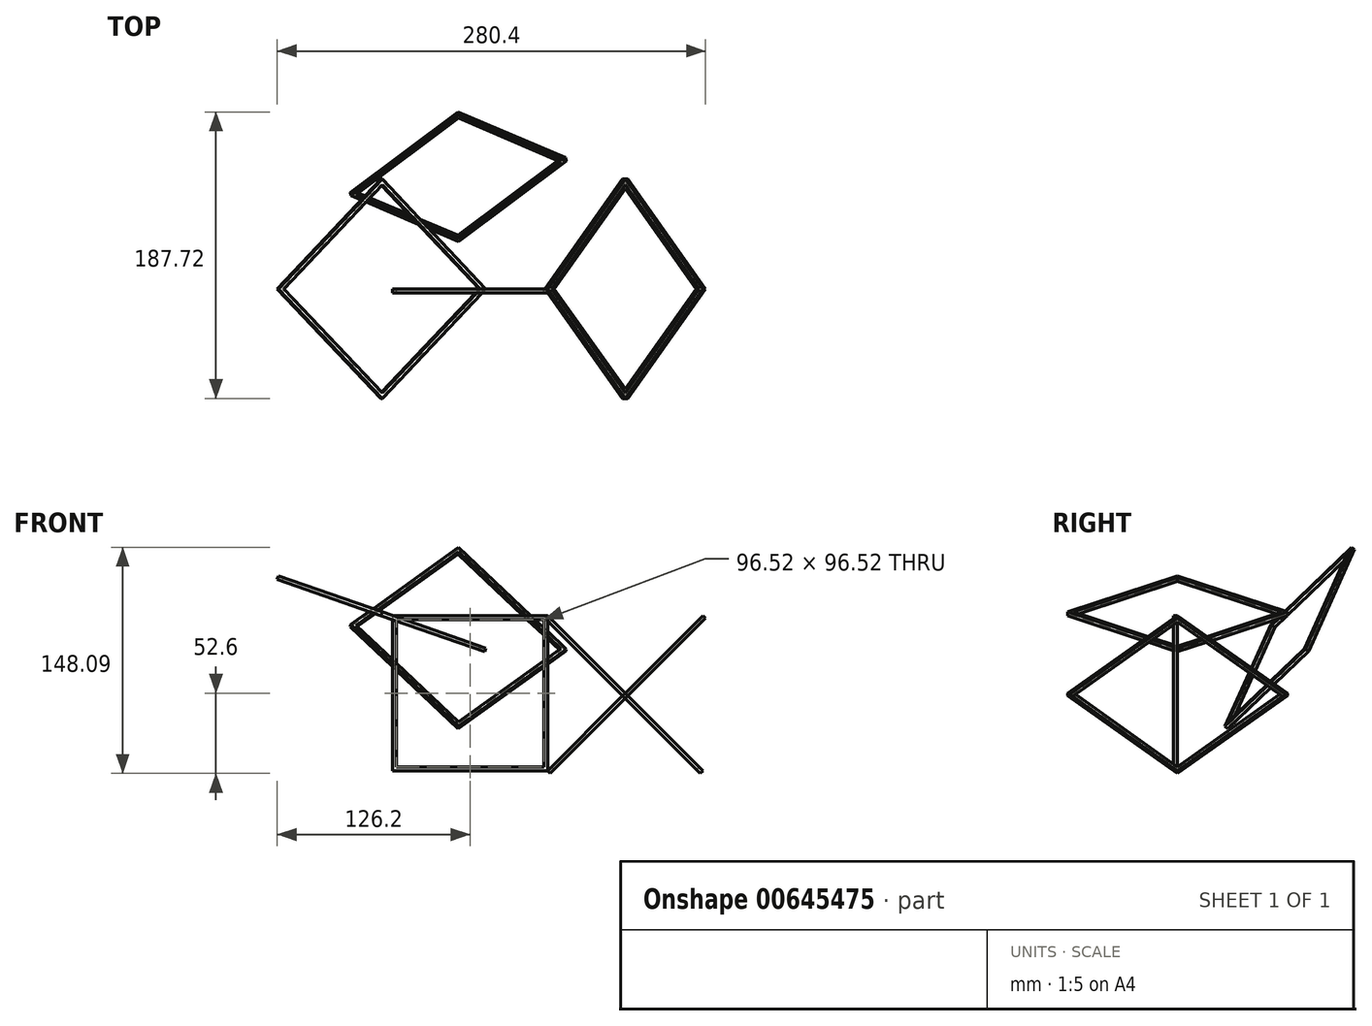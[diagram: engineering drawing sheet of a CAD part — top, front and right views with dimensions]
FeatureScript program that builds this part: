
annotation { "Feature Type Name" : "Feature", "Feature Type Description" : "" }
export const myFeature = defineFeature(function(context is Context, id is Id, definition is map)
    precondition{}
    {
        {
            var Q0;
            Q0=qCreatedBy(makeId("Front.planeOp"),FACE);
            var sketch = newSketch(context, id + "F0", { "sketchPlane" : qUnion([Q0])});
            skLineSegment(sketch, "E0.bottom", {"start": v(-48.26, 48.26) * mm, "end": v(48.26, 48.26) * mm});
            skLineSegment(sketch, "E0.top", {"start": v(-48.26, -48.26) * mm, "end": v(48.26, -48.26) * mm});
            skLineSegment(sketch, "E0.left", {"start": v(-48.26, 48.26) * mm, "end": v(-48.26, -48.26) * mm});
            skLineSegment(sketch, "E0.right", {"start": v(48.26, 48.26) * mm, "end": v(48.26, -48.26) * mm});
            skPoint(sketch, "E0.middle", {"position": v(0, 0) * mm});
            skLineSegment(sketch, "E1.bottom", {"start": v(-50.8, 50.8) * mm, "end": v(50.8, 50.8) * mm});
            skLineSegment(sketch, "E1.top", {"start": v(-50.8, -50.8) * mm, "end": v(50.8, -50.8) * mm});
            skLineSegment(sketch, "E1.left", {"start": v(-50.8, 50.8) * mm, "end": v(-50.8, -50.8) * mm});
            skLineSegment(sketch, "E1.right", {"start": v(50.8, 50.8) * mm, "end": v(50.8, -50.8) * mm});
            skSolve(sketch);
        }
        {
            var Q0;
            Q0=makeQuery(id+"F0.imprint","IMPRINT",FACE,{"disambiguationData":[TD([[makeQuery(id+"F0.imprint","IMPRINT",EDGE,{"derivedFrom":sQuery(id+"F0.wireOp",EDGE,"E0.bottom")}),1.0]])]});
            extrude(context, id + "F1", {"entities" : qUnion([Q0]), "depth" : 2.54 * mm, "offsetDistance" : 25.4 * mm});
        }
        {
            var Q0;
            Q0=makeQuery(id+"F1.opExtrude","SWEPT_EDGE",EDGE,{"disambiguationData":[OSD([sQuery(id+"F0.wireOp",EDGE,"E1.bottom"),sQuery(id+"F0.wireOp",EDGE,"E1.right")])]});
            cPlane(context, id + "F2", {"entities" : qUnion([Q0]), "cplaneType" : CPlaneType.LINE_ANGLE, "offset" : 25.4 * mm, "angle" : 45 * degree, "width" : 152.4 * mm, "height" : 152.4 * mm});
        }
        {
            var Q0;
            Q0=qCreatedBy(id+"F2.planeOp",FACE);
            var sketch = newSketch(context, id + "F3", { "sketchPlane" : qUnion([Q0])});
            skLineSegment(sketch, "E2", {"start": v(0, 0) * mm, "end": v(-71.84, -71.84) * mm});
            skLineSegment(sketch, "E3", {"start": v(-71.84, -71.84) * mm, "end": v(0, -143.68) * mm});
            skLineSegment(sketch, "E4", {"start": v(0, -143.68) * mm, "end": v(71.84, -71.84) * mm});
            skLineSegment(sketch, "E5", {"start": v(71.84, -71.84) * mm, "end": v(0, 0) * mm});
            skLineSegment(sketch, "E6", {"start": v(-68.25, -71.84) * mm, "end": v(0, -140.1) * mm});
            skLineSegment(sketch, "E7", {"start": v(0, -140.1) * mm, "end": v(68.25, -71.84) * mm});
            skLineSegment(sketch, "E8", {"start": v(68.25, -71.84) * mm, "end": v(0, -3.6) * mm});
            skLineSegment(sketch, "E9", {"start": v(0, -3.6) * mm, "end": v(-68.25, -71.84) * mm});
            skSolve(sketch);
        }
        {
            var Q0;
            Q0=makeQuery(id+"F3.imprint","IMPRINT",FACE,{"disambiguationData":[TD([[makeQuery(id+"F3.imprint","IMPRINT",EDGE,{"derivedFrom":sQuery(id+"F3.wireOp",EDGE,"E2")}),1.0]])]});
            extrude(context, id + "F4", {"entities" : qUnion([Q0]), "oppositeDirection" : true, "depth" : 2.54 * mm, "offsetDistance" : 25.4 * mm});
        }
        {
            var Q0;
            Q0=makeQuery(id+"F1.opExtrude","CAP_VERTEX",VERTEX,{"disambiguationData":[OSD([sQuery(id+"F0.wireOp",EDGE,"E1.bottom"),sQuery(id+"F0.wireOp",EDGE,"E1.left")])],"isStart":true});
            var Q1;
            Q1=makeQuery(id+"F1.opExtrude","CAP_VERTEX",VERTEX,{"disambiguationData":[OSD([sQuery(id+"F0.wireOp",EDGE,"E1.bottom"),sQuery(id+"F0.wireOp",EDGE,"E1.left")])],"isStart":false});
            var Q2;
            Q2=makeQuery(id+"F4.opExtrude","CAP_VERTEX",VERTEX,{"disambiguationData":[OSD([sQuery(id+"F3.wireOp",EDGE,"E2"),sQuery(id+"F3.wireOp",EDGE,"E3")])],"isStart":false});
            cPlane(context, id + "F5", {"entities" : qUnion([Q0, Q1, Q2]), "cplaneType" : CPlaneType.THREE_POINT, "offset" : 25.4 * mm, "width" : 152.4 * mm, "height" : 152.4 * mm});
        }
        {
            var Q0;
            Q0=qCreatedBy(id+"F5.planeOp",FACE);
            var sketch = newSketch(context, id + "F6", { "sketchPlane" : qUnion([Q0])});
            skLineSegment(sketch, "E10", {"start": v(-71.84, 71.84) * mm, "end": v(-143.68, 0) * mm});
            skLineSegment(sketch, "E11", {"start": v(-143.68, 0) * mm, "end": v(-71.84, -71.84) * mm});
            skLineSegment(sketch, "E12", {"start": v(-71.84, -71.84) * mm, "end": v(0, 0) * mm});
            skLineSegment(sketch, "E13", {"start": v(0, 0) * mm, "end": v(-71.84, 71.84) * mm});
            skLineSegment(sketch, "E14", {"start": v(-140.1, 0) * mm, "end": v(-71.84, -68.25) * mm});
            skLineSegment(sketch, "E15", {"start": v(-71.84, -68.25) * mm, "end": v(-3.6, 0) * mm});
            skLineSegment(sketch, "E16", {"start": v(-3.6, 0) * mm, "end": v(-71.84, 68.25) * mm});
            skLineSegment(sketch, "E17", {"start": v(-71.84, 68.25) * mm, "end": v(-140.1, 0) * mm});
            skSolve(sketch);
        }
        {
            var Q0;
            Q0 = qSketchRegion(id + "F6", true);
            extrude(context, id + "F7", {"entities" : qUnion([Q0]), "depth" : 2.54 * mm, "offsetDistance" : 25.4 * mm});
        }
        {
            var Q0;
            Q0=makeQuery(id+"F4.opExtrude","CAP_VERTEX",VERTEX,{"disambiguationData":[OSD([sQuery(id+"F3.wireOp",EDGE,"E4"),sQuery(id+"F3.wireOp",EDGE,"E5")])],"isStart":false});
            var Q1;
            Q1=makeQuery(id+"F4.opExtrude","CAP_VERTEX",VERTEX,{"disambiguationData":[OSD([sQuery(id+"F3.wireOp",EDGE,"E4"),sQuery(id+"F3.wireOp",EDGE,"E5")])],"isStart":true});
            var Q2;
            Q2=makeQuery(id+"F1.opExtrude","CAP_VERTEX",VERTEX,{"disambiguationData":[OSD([sQuery(id+"F0.wireOp",EDGE,"E1.top"),sQuery(id+"F0.wireOp",EDGE,"E1.right")])],"isStart":true});
            cPlane(context, id + "F8", {"entities" : qUnion([Q0, Q1, Q2]), "cplaneType" : CPlaneType.THREE_POINT, "offset" : 25.4 * mm, "width" : 152.4 * mm, "height" : 152.4 * mm});
        }
        {
            var Q0;
            Q0=qCreatedBy(id+"F8.planeOp",FACE);
            var sketch = newSketch(context, id + "F9", { "sketchPlane" : qUnion([Q0])});
            skLineSegment(sketch, "E18", {"start": v(0, 143.68) * mm, "end": v(-71.84, 71.84) * mm});
            skLineSegment(sketch, "E19", {"start": v(-71.84, 71.84) * mm, "end": v(0, 0) * mm});
            skLineSegment(sketch, "E20", {"start": v(0, 0) * mm, "end": v(71.84, 71.84) * mm});
            skLineSegment(sketch, "E21", {"start": v(71.84, 71.84) * mm, "end": v(0, 143.68) * mm});
            skLineSegment(sketch, "E22", {"start": v(-68.25, 71.84) * mm, "end": v(0, 3.6) * mm});
            skLineSegment(sketch, "E23", {"start": v(0, 3.6) * mm, "end": v(68.25, 71.84) * mm});
            skLineSegment(sketch, "E24", {"start": v(68.25, 71.84) * mm, "end": v(0, 140.1) * mm});
            skLineSegment(sketch, "E25", {"start": v(0, 140.1) * mm, "end": v(-68.25, 71.84) * mm});
            skSolve(sketch);
        }
        {
            var Q0;
            Q0=makeQuery(id+"F9.imprint","IMPRINT",FACE,{"disambiguationData":[TD([[makeQuery(id+"F9.imprint","IMPRINT",EDGE,{"derivedFrom":sQuery(id+"F9.wireOp",EDGE,"E18")}),1.0]])]});
            extrude(context, id + "F10", {"entities" : qUnion([Q0]), "oppositeDirection" : true, "depth" : 2.54 * mm, "offsetDistance" : 25.4 * mm});
        }
        {
            var Q0;
            Q0=makeQuery(id+"F7.opExtrude","CAP_VERTEX",VERTEX,{"disambiguationData":[OSD([sQuery(id+"F6.wireOp",EDGE,"E11"),sQuery(id+"F6.wireOp",EDGE,"E12")])],"isStart":true});
            var Q1;
            Q1=makeQuery(id+"F10.opExtrude","CAP_VERTEX",VERTEX,{"disambiguationData":[OSD([sQuery(id+"F9.wireOp",EDGE,"E18"),sQuery(id+"F9.wireOp",EDGE,"E19")])],"isStart":false});
            var Q2;
            Q2=makeQuery(id+"F1.opExtrude","CAP_VERTEX",VERTEX,{"disambiguationData":[OSD([sQuery(id+"F0.wireOp",EDGE,"E1.top"),sQuery(id+"F0.wireOp",EDGE,"E1.left")])],"isStart":true});
            cPlane(context, id + "F11", {"entities" : qUnion([Q0, Q1, Q2]), "cplaneType" : CPlaneType.THREE_POINT, "offset" : 25.4 * mm, "width" : 152.4 * mm, "height" : 152.4 * mm});
        }
        {
            var Q0;
            Q0=qCreatedBy(id+"F11.planeOp",FACE);
            var sketch = newSketch(context, id + "F12", { "sketchPlane" : qUnion([Q0])});
            skLineSegment(sketch, "E26", {"start": v(0, 143.68) * mm, "end": v(-71.84, 71.84) * mm});
            skLineSegment(sketch, "E27", {"start": v(-71.84, 71.84) * mm, "end": v(0, 0) * mm});
            skLineSegment(sketch, "E28", {"start": v(0, 0) * mm, "end": v(71.84, 71.84) * mm});
            skLineSegment(sketch, "E29", {"start": v(71.84, 71.84) * mm, "end": v(0, 143.68) * mm});
            skLineSegment(sketch, "E30", {"start": v(-68.25, 71.84) * mm, "end": v(0, 3.6) * mm});
            skLineSegment(sketch, "E31", {"start": v(0, 3.6) * mm, "end": v(68.25, 71.84) * mm});
            skLineSegment(sketch, "E32", {"start": v(68.25, 71.84) * mm, "end": v(0, 140.1) * mm});
            skLineSegment(sketch, "E33", {"start": v(0, 140.1) * mm, "end": v(-68.25, 71.84) * mm});
            skSolve(sketch);
        }
        {
            var Q0;
            Q0=makeQuery(id+"F12.imprint","IMPRINT",FACE,{"disambiguationData":[TD([[makeQuery(id+"F12.imprint","IMPRINT",EDGE,{"derivedFrom":sQuery(id+"F12.wireOp",EDGE,"E26")}),1.0]])]});
            extrude(context, id + "F13", {"entities" : qUnion([Q0]), "oppositeDirection" : true, "depth" : 2.54 * mm, "offsetDistance" : 25.4 * mm});
        }
        {
            var Q0;
            Q0=makeQuery(id+"F4.opExtrude","CAP_VERTEX",VERTEX,{"disambiguationData":[OSD([sQuery(id+"F3.wireOp",EDGE,"E3"),sQuery(id+"F3.wireOp",EDGE,"E4")])],"isStart":true});
            var Q1;
            Q1=makeQuery(id+"F10.opExtrude","CAP_VERTEX",VERTEX,{"disambiguationData":[OSD([sQuery(id+"F9.wireOp",EDGE,"E18"),sQuery(id+"F9.wireOp",EDGE,"E21")])],"isStart":true});
            var Q2;
            Q2=makeQuery(id+"F13.opExtrude","CAP_VERTEX",VERTEX,{"disambiguationData":[OSD([sQuery(id+"F12.wireOp",EDGE,"E26"),sQuery(id+"F12.wireOp",EDGE,"E29")])],"isStart":false});
            cPlane(context, id + "F14", {"entities" : qUnion([Q0, Q1, Q2]), "cplaneType" : CPlaneType.THREE_POINT, "offset" : 25.4 * mm, "width" : 152.4 * mm, "height" : 152.4 * mm});
        }
    });
